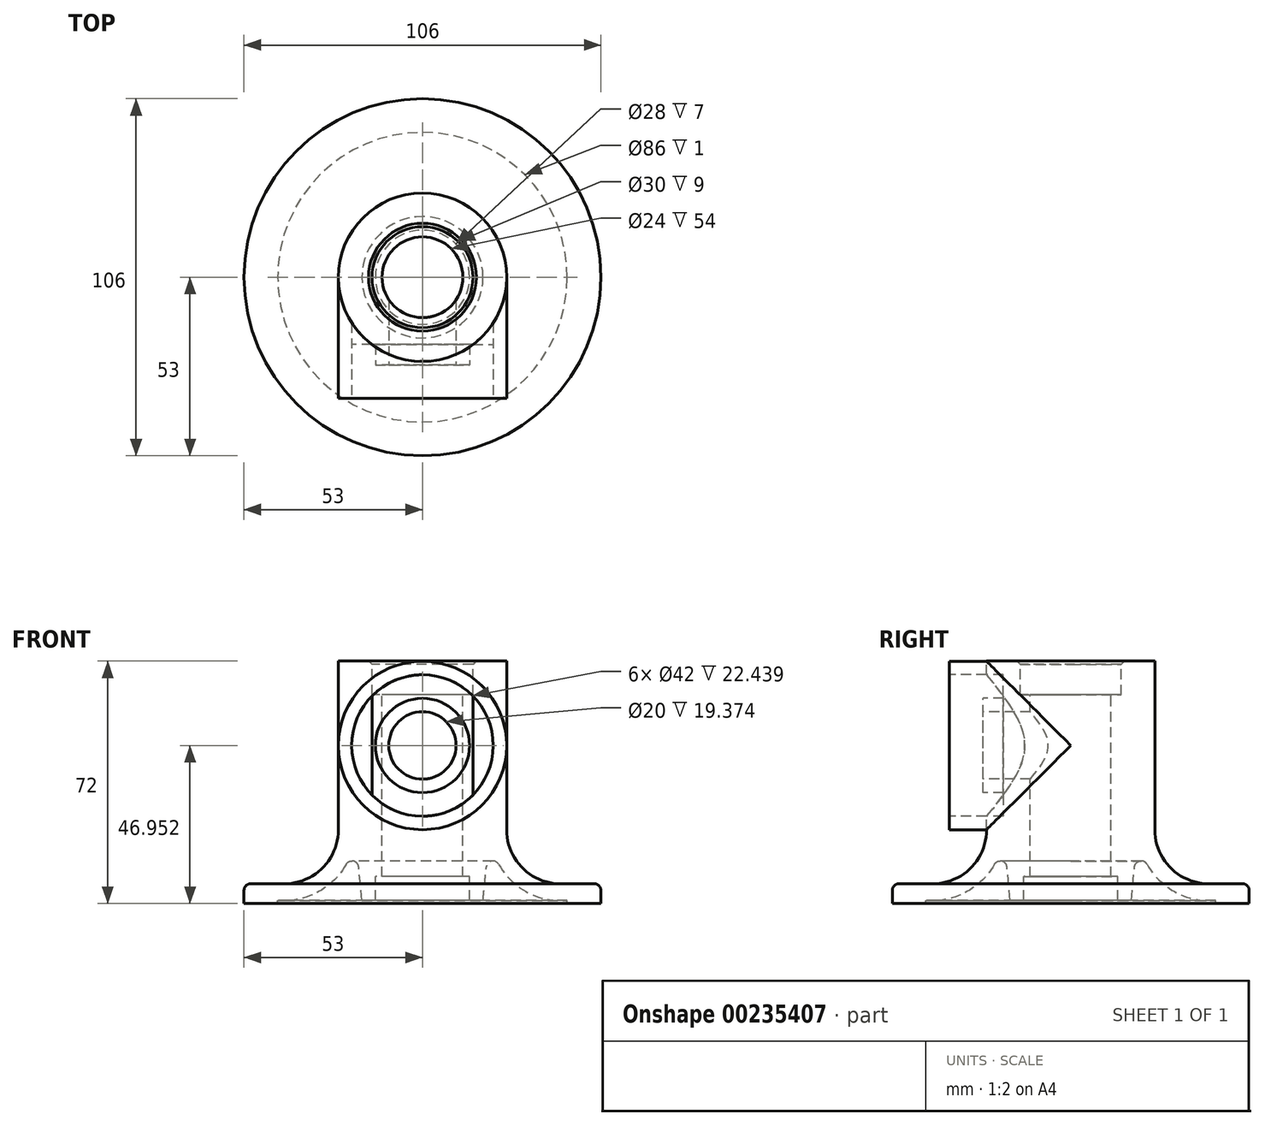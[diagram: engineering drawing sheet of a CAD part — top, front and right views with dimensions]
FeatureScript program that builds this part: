
annotation { "Feature Type Name" : "Feature", "Feature Type Description" : "" }
export const myFeature = defineFeature(function(context is Context, id is Id, definition is map)
    precondition{}
    {
        {
            var Q0;
            Q0=qCreatedBy(makeId("Front.planeOp"),FACE);
            var sketch = newSketch(context, id + "F0", { "sketchPlane" : qUnion([Q0])});
            skLineSegment(sketch, "E0", {"start": v(0, 69.65) * mm, "end": v(0, -71.3) * mm, "construction": true});
            skLineSegment(sketch, "E1", {"start": v(14, 1) * mm, "end": v(14, 8) * mm});
            skLineSegment(sketch, "E2", {"start": v(14, 8) * mm, "end": v(12, 8) * mm});
            skLineSegment(sketch, "E3", {"start": v(12, 8) * mm, "end": v(12, 62) * mm});
            skLineSegment(sketch, "E4", {"start": v(12, 62) * mm, "end": v(15, 62) * mm});
            skLineSegment(sketch, "E5", {"start": v(15, 62) * mm, "end": v(15, 72) * mm});
            skLineSegment(sketch, "E6", {"start": v(15, 72) * mm, "end": v(25, 72) * mm});
            skLineSegment(sketch, "E7", {"start": v(25, 72) * mm, "end": v(25, 21.9) * mm});
            skLineSegment(sketch, "E8", {"start": v(41, 5.9) * mm, "end": v(53, 5.9) * mm});
            skLineSegment(sketch, "E9", {"start": v(53, 5.9) * mm, "end": v(53, 0) * mm});
            skLineSegment(sketch, "E10", {"start": v(53, 0) * mm, "end": v(43, 0) * mm});
            skArc(sketch, "E11", {"start": v(25, 21.9) * mm, "mid": v(29.69, 10.6) * mm, "end": v(41, 5.9) * mm});
            skLineSegment(sketch, "E12", {"start": v(18, 1) * mm, "end": v(18.94, 10.85) * mm});
            skLineSegment(sketch, "E13", {"start": v(14, 1) * mm, "end": v(18, 1) * mm});
            skLineSegment(sketch, "E14", {"start": v(43, 0) * mm, "end": v(43, 1) * mm});
            skArc(sketch, "E15", {"start": v(22.68, 11.64) * mm, "mid": v(31.26, 3.3) * mm, "end": v(43, 1) * mm});
            skPoint(sketch, "E16.visualSharp", {"position": v(20, 21.9) * mm});
            skArc(sketch, "E16.filletArc", {"start": v(22.68, 11.64) * mm, "mid": v(20.52, 12.62) * mm, "end": v(18.94, 10.85) * mm});
            skSolve(sketch);
        }
        {
            var Q0;
            Q0=makeQuery(id+"F0.imprint","IMPRINT",FACE,{"disambiguationData":[TD([[makeQuery(id+"F0.imprint","IMPRINT",EDGE,{"derivedFrom":sQuery(id+"F0.wireOp",EDGE,"E1")}),-1.0]])]});
            var Q1;
            Q1=sQuery(id+"F0.wireOp",EDGE,"E0");
            revolve(context, id + "F1", {"entities" : qUnion([Q0]), "axis" : qUnion([Q1]), "revolveType" : RevolveType.FULL});
        }
        {
            var Q0;
            Q0=makeQuery(id+"F1.opRevolve","SWEPT_EDGE",EDGE,{"disambiguationData":[OSD([sQuery(id+"F0.wireOp",EDGE,"E5"),sQuery(id+"F0.wireOp",EDGE,"E6")])]});
            chamfer(context, id + "F2", {"entities" : qUnion([Q0]), "chamferType" : ChamferType.OFFSET_ANGLE, "width" : 1 * mm, "oppositeDirection" : false, "angle" : 45 * degree, "tangentPropagation" : true});
        }
        {
            var Q0;
            Q0=makeQuery(id+"F1.opRevolve","SWEPT_EDGE",EDGE,{"disambiguationData":[OSD([sQuery(id+"F0.wireOp",EDGE,"E8"),sQuery(id+"F0.wireOp",EDGE,"E9")])]});
            fillet(context, id + "F3", {"entities" : qUnion([Q0]), "radius" : 2 * mm, "tangentPropagation" : true, "allowEdgeOverflow" : false});
        }
        {
            var Q0;
            Q0=qCreatedBy(makeId("Front.planeOp"),FACE);
            cPlane(context, id + "F4", {"entities" : qUnion([Q0]), "cplaneType" : CPlaneType.OFFSET, "offset" : 36 * mm, "width" : 150 * mm, "height" : 150 * mm});
        }
        {
            var Q0;
            Q0=qCreatedBy(id+"F4.planeOp",FACE);
            var sketch = newSketch(context, id + "F5", { "sketchPlane" : qUnion([Q0])});
            skLineSegment(sketch, "E17", {"start": v(25, 72) * mm, "end": v(25, 21.9) * mm});
            skLineSegment(sketch, "E18", {"start": v(-25, 21.9) * mm, "end": v(-25, 72) * mm});
            skLineSegment(sketch, "E19", {"start": v(-49.47, 46.95) * mm, "end": v(62.47, 46.95) * mm, "construction": true});
            skPoint(sketch, "E19.startSnap0", {"position": v(-25, 46.95) * mm});
            skLineSegment(sketch, "E20", {"start": v(0, 46.95) * mm, "end": v(0, 83.73) * mm, "construction": true});
            skLineSegment(sketch, "E21", {"start": v(0, 83.73) * mm, "end": v(0, 21.05) * mm, "construction": true});
            skCircle(sketch, "E22", {"center": v(0, 46.95) * mm, "radius": 21 * mm});
            skCircle(sketch, "E23", {"center": v(0, 46.95) * mm, "radius": 25 * mm});
            skCircle(sketch, "E24", {"center": v(0, 46.95) * mm, "radius": 10 * mm});
            skCircle(sketch, "E25", {"center": v(0, 46.95) * mm, "radius": 14 * mm});
            skSolve(sketch);
        }
        {
            var Q0;
            Q0=makeQuery(id+"F5.imprint","IMPRINT",FACE,{"disambiguationData":[TD([[makeQuery(id+"F5.imprint","IMPRINT",EDGE,{"derivedFrom":sQuery(id+"F5.wireOp",EDGE,"E22")}),-1.0]])]});
            extrude(context, id + "F6", {"entities" : qUnion([Q0]), "endBound" : BoundingType.UP_TO_NEXT, "oppositeDirection" : true, "depth" : 25 * mm});
        }
        {
            var Q0;
            Q0=makeQuery(id+"F5.imprint","IMPRINT",FACE,{"disambiguationData":[TD([[makeQuery(id+"F5.imprint","IMPRINT",EDGE,{"derivedFrom":sQuery(id+"F5.wireOp",EDGE,"E24")}),1.0]])]});
            var Q1;
            Q1=makeQuery(id+"F1.opRevolve","SWEPT_FACE",FACE,{"disambiguationData":[OSD([sQuery(id+"F0.wireOp",EDGE,"E3")])]});
            extrude(context, id + "F7", {"entities" : qUnion([Q0]), "operationType" : NewBodyOperationType.REMOVE, "endBound" : BoundingType.UP_TO_SURFACE, "oppositeDirection" : true, "endBoundEntityFace" : qUnion([Q1]), "depth" : 25 * mm});
        }
        {
            var Q0;
            Q0=makeQuery(id+"F5.imprint","IMPRINT",FACE,{"disambiguationData":[TD([[makeQuery(id+"F5.imprint","IMPRINT",EDGE,{"derivedFrom":sQuery(id+"F5.wireOp",EDGE,"E24")}),-1.0]])]});
            var Q1;
            Q1=makeQuery(id+"F1.opRevolve","SWEPT_FACE",FACE,{"disambiguationData":[OSD([sQuery(id+"F0.wireOp",EDGE,"E7")])]});
            extrude(context, id + "F8", {"entities" : qUnion([Q0]), "operationType" : NewBodyOperationType.ADD, "endBound" : BoundingType.UP_TO_SURFACE, "oppositeDirection" : true, "endBoundEntityFace" : qUnion([Q1]), "depth" : 25 * mm});
        }
        {
            var Q0;
            Q0=makeQuery(id+"F5.imprint","IMPRINT",FACE,{"disambiguationData":[TD([[makeQuery(id+"F5.imprint","IMPRINT",EDGE,{"derivedFrom":sQuery(id+"F5.wireOp",EDGE,"E24")}),-1.0]])]});
            extrude(context, id + "F9", {"entities" : qUnion([Q0]), "operationType" : NewBodyOperationType.REMOVE, "oppositeDirection" : true, "depth" : 10 * mm});
        }
        {
            var Q0;
            Q0=makeQuery(id+"F5.imprint","IMPRINT",FACE,{"disambiguationData":[TD([[makeQuery(id+"F5.imprint","IMPRINT",EDGE,{"derivedFrom":sQuery(id+"F5.wireOp",EDGE,"E22")}),1.0]])]});
            var Q1;
            Q1=makeQuery(id+"F1.opRevolve","SWEPT_FACE",FACE,{"disambiguationData":[OSD([sQuery(id+"F0.wireOp",EDGE,"E7")])]});
            extrude(context, id + "F10", {"entities" : qUnion([Q0]), "endBound" : BoundingType.UP_TO_SURFACE, "oppositeDirection" : true, "endBoundEntityFace" : qUnion([Q1]), "depth" : 16 * mm});
        }
        {
            var Q0;
            Q0=makeQuery(id+"F5.imprint","IMPRINT",FACE,{"disambiguationData":[TD([[makeQuery(id+"F5.imprint","IMPRINT",EDGE,{"derivedFrom":sQuery(id+"F5.wireOp",EDGE,"E22")}),1.0]])]});
            extrude(context, id + "F11", {"entities" : qUnion([Q0]), "operationType" : NewBodyOperationType.REMOVE, "oppositeDirection" : true, "depth" : 16 * mm});
        }
    });
